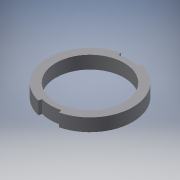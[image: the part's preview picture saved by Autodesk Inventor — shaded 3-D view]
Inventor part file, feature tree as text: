
AUTODESK INVENTOR PART (.ipt)
format: ipt  version: 2016 (Build 200138000, 138)  size: 118,272 bytes
history: native  units: mm
features: extrude x2, sketch x2
ambient origin geometry x8: Origin, YZ Plane, XZ Plane, XY Plane, X Axis, Y Axis, Z Axis, Center Point
bodies: Solid1 (feature_tree)
feature tree (4):
  extrude  "Extrusion1"  Depth=40.0mm
  extrude  "Extrusion2"  Depth=6.0mm
  sketch  "Sketch1"  dims[d0=32.0mm d1=40.0mm]
  sketch  "Sketch2"  dims[d2=6.0mm d3=0.0mm d4=9.0mm d5=1.5mm d6=6.0mm d7=0.0mm]
